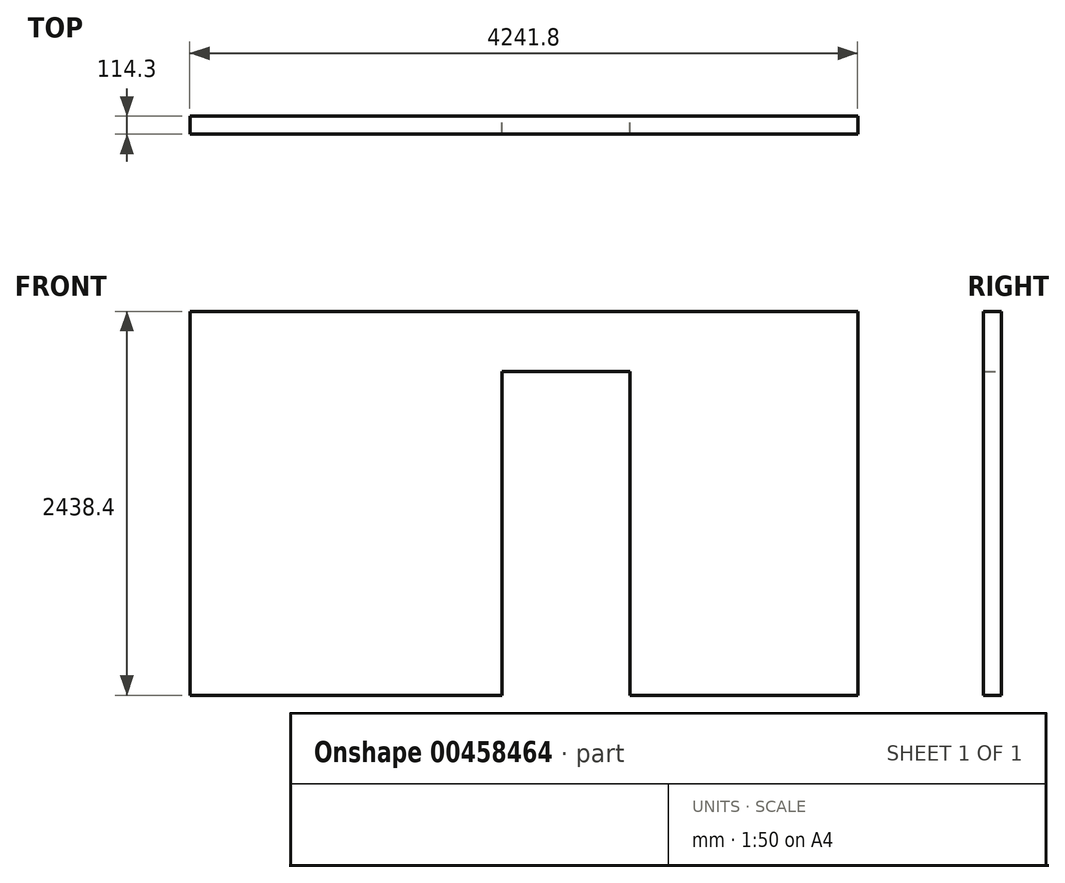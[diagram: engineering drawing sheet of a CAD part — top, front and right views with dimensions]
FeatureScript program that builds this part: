
annotation { "Feature Type Name" : "Feature", "Feature Type Description" : "" }
export const myFeature = defineFeature(function(context is Context, id is Id, definition is map)
    precondition{}
    {
        {
            var Q0;
            Q0=qCreatedBy(makeId("Front.planeOp"),FACE);
            var sketch = newSketch(context, id + "F0", { "sketchPlane" : qUnion([Q0])});
            skLineSegment(sketch, "E0.bottom", {"start": v(-2337.44, -1194.82) * mm, "end": v(-356.24, -1194.82) * mm});
            skLineSegment(sketch, "E0.top", {"start": v(-2337.44, 1243.58) * mm, "end": v(-356.24, 1243.58) * mm});
            skLineSegment(sketch, "E0.left", {"start": v(-2337.44, -1194.82) * mm, "end": v(-2337.44, 1243.58) * mm});
            skLineSegment(sketch, "E0.right", {"start": v(-356.24, -1194.82) * mm, "end": v(-356.24, 1243.58) * mm});
            skLineSegment(sketch, "E1.bottom", {"start": v(-356.24, 1243.58) * mm, "end": v(456.56, 1243.58) * mm});
            skLineSegment(sketch, "E1.top", {"start": v(-356.24, 862.58) * mm, "end": v(456.56, 862.58) * mm});
            skLineSegment(sketch, "E1.left", {"start": v(-356.24, 1243.58) * mm, "end": v(-356.24, 862.58) * mm});
            skLineSegment(sketch, "E1.right", {"start": v(456.56, 1243.58) * mm, "end": v(456.56, 862.58) * mm});
            skLineSegment(sketch, "E2.bottom", {"start": v(456.56, 1243.58) * mm, "end": v(1904.36, 1243.58) * mm});
            skLineSegment(sketch, "E2.top", {"start": v(456.56, -1194.82) * mm, "end": v(1904.36, -1194.82) * mm});
            skLineSegment(sketch, "E2.left", {"start": v(456.56, 1243.58) * mm, "end": v(456.56, -1194.82) * mm});
            skLineSegment(sketch, "E2.right", {"start": v(1904.36, 1243.58) * mm, "end": v(1904.36, -1194.82) * mm});
            skSolve(sketch);
        }
        {
            var Q0;
            Q0=makeQuery(id+"F0.imprint","IMPRINT",FACE,{"disambiguationData":[TD([[makeQuery(id+"F0.imprint","IMPRINT",EDGE,{"derivedFrom":sQuery(id+"F0.wireOp",EDGE,"E0.bottom")}),1.0]])]});
            var Q1;
            {var subQ0=sQuery(id+"F0.wireOp",EDGE,"E1.bottom");Q1=makeQuery(id+"F0.imprint","IMPRINT",FACE,{"disambiguationData":[TD([[makeQuery(id+"F0.imprint","IMPRINT",EDGE,{"derivedFrom":subQ0}),-1.0]])]});}
            var Q2;
            {var subQ3=sQuery(id+"F0.wireOp",EDGE,"E2.bottom");Q2=makeQuery(id+"F0.imprint","IMPRINT",FACE,{"disambiguationData":[TD([[makeQuery(id+"F0.imprint","IMPRINT",EDGE,{"derivedFrom":subQ3}),-1.0]])]});}
            extrude(context, id + "F1", {"entities" : qUnion([Q0, Q1, Q2]), "depth" : 114.3 * mm});
        }
    });
